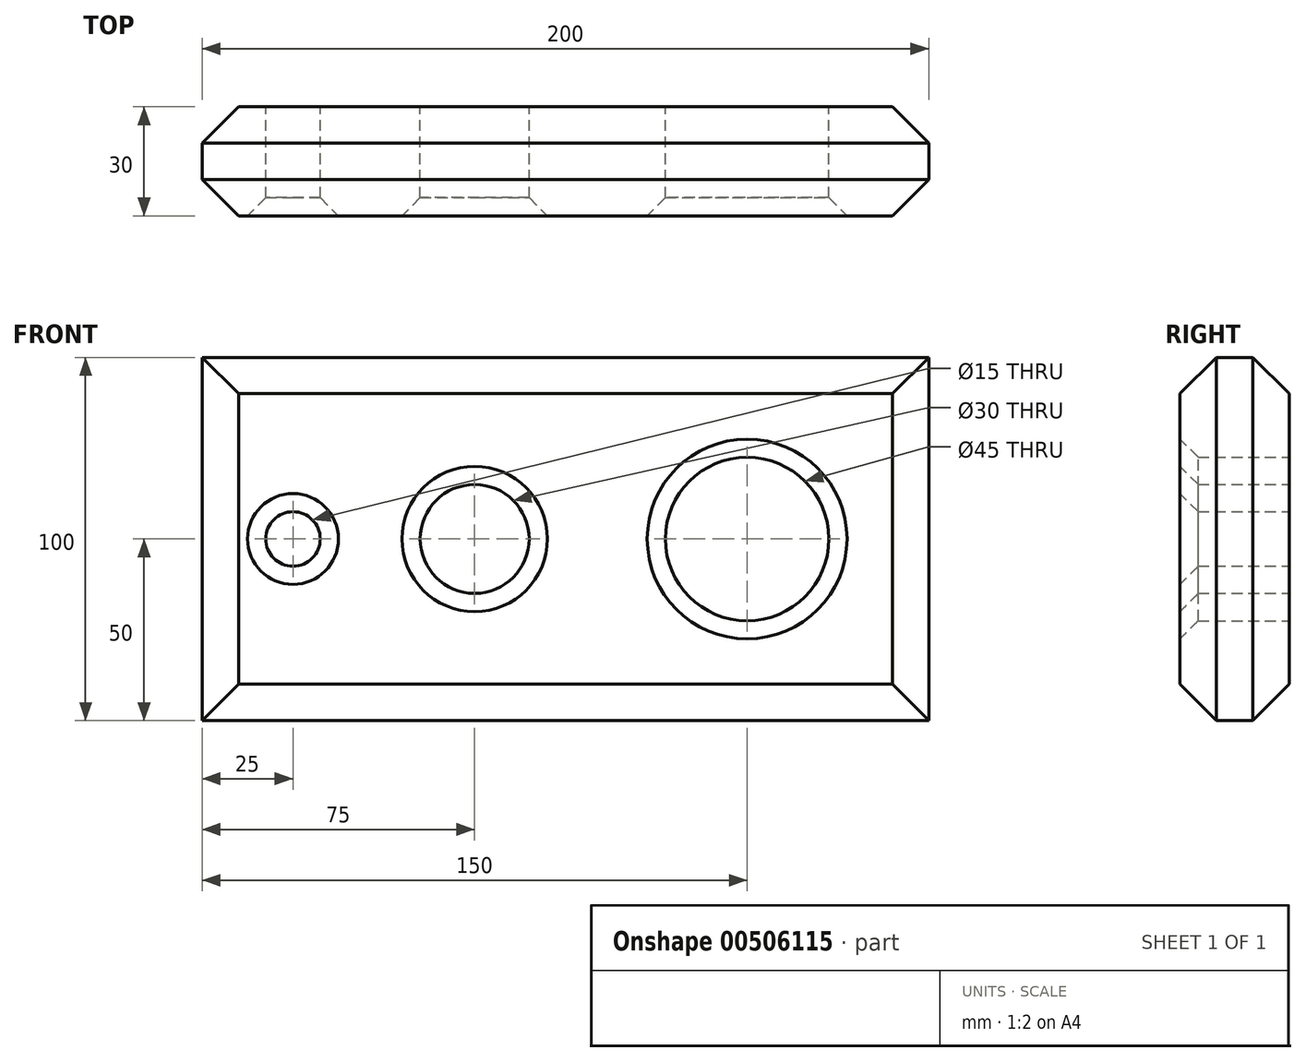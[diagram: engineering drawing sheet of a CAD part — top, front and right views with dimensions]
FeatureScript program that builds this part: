
annotation { "Feature Type Name" : "Feature", "Feature Type Description" : "" }
export const myFeature = defineFeature(function(context is Context, id is Id, definition is map)
    precondition{}
    {
        {
            var Q0;
            Q0=qCreatedBy(makeId("Front.planeOp"),FACE);
            var sketch = newSketch(context, id + "F0", { "sketchPlane" : qUnion([Q0])});
            skLineSegment(sketch, "E0.bottom", {"start": v(-100, 50) * mm, "end": v(100, 50) * mm});
            skLineSegment(sketch, "E0.top", {"start": v(-100, -50) * mm, "end": v(100, -50) * mm});
            skLineSegment(sketch, "E0.left", {"start": v(-100, 50) * mm, "end": v(-100, -50) * mm});
            skLineSegment(sketch, "E0.right", {"start": v(100, 50) * mm, "end": v(100, -50) * mm});
            skLineSegment(sketch, "E1", {"start": v(-100, 0) * mm, "end": v(-75, 0) * mm});
            skPoint(sketch, "E1.endSnap0", {"position": v(-100, 0) * mm});
            skLineSegment(sketch, "E2", {"start": v(-75, 0) * mm, "end": v(-25, 0) * mm});
            skLineSegment(sketch, "E3", {"start": v(-25, 0) * mm, "end": v(50, 0) * mm});
            skCircle(sketch, "E4", {"center": v(-75, 0) * mm, "radius": 7.5 * mm});
            skCircle(sketch, "E5", {"center": v(-25, 0) * mm, "radius": 15 * mm});
            skCircle(sketch, "E6", {"center": v(50, 0) * mm, "radius": 22.5 * mm});
            skSolve(sketch);
        }
        {
            var Q0;
            {var subQ3=sQuery(id+"F0.wireOp",EDGE,"E0.bottom");Q0=makeQuery(id+"F0.imprint","IMPRINT",FACE,{"disambiguationData":[TD([[makeQuery(id+"F0.imprint","IMPRINT",EDGE,{"derivedFrom":subQ3}),-1.0]])]});}
            extrude(context, id + "F1", {"entities" : qUnion([Q0]), "depth" : 30 * mm});
        }
        {
            var Q0;
            Q0=makeQuery(id+"F1.opExtrude","CAP_EDGE",EDGE,{"disambiguationData":[OSD([sQuery(id+"F0.wireOp",EDGE,"E0.left")])],"isStart":false});
            var Q1;
            Q1=makeQuery(id+"F1.opExtrude","CAP_EDGE",EDGE,{"disambiguationData":[OSD([sQuery(id+"F0.wireOp",EDGE,"E0.top")])],"isStart":false});
            var Q2;
            Q2=makeQuery(id+"F1.opExtrude","CAP_EDGE",EDGE,{"disambiguationData":[OSD([sQuery(id+"F0.wireOp",EDGE,"E0.right")])],"isStart":false});
            var Q3;
            Q3=makeQuery(id+"F1.opExtrude","CAP_EDGE",EDGE,{"disambiguationData":[OSD([sQuery(id+"F0.wireOp",EDGE,"E0.bottom")])],"isStart":false});
            chamfer(context, id + "F2", {"entities" : qUnion([Q0, Q1, Q2, Q3]), "width" : 10 * mm, "tangentPropagation" : true});
        }
        {
            var Q0;
            Q0=makeQuery(id+"F1.opExtrude","CAP_EDGE",EDGE,{"disambiguationData":[OSD([sQuery(id+"F0.wireOp",EDGE,"E4")])],"isStart":false});
            var Q1;
            Q1=makeQuery(id+"F1.opExtrude","CAP_EDGE",EDGE,{"disambiguationData":[OSD([sQuery(id+"F0.wireOp",EDGE,"E5")])],"isStart":false});
            var Q2;
            Q2=makeQuery(id+"F1.opExtrude","CAP_EDGE",EDGE,{"disambiguationData":[OSD([sQuery(id+"F0.wireOp",EDGE,"E6")])],"isStart":false});
            chamfer(context, id + "F3", {"entities" : qUnion([Q0, Q1, Q2]), "width" : 5 * mm, "tangentPropagation" : true});
        }
        {
            var Q0;
            Q0=makeQuery(id+"F1.opExtrude","CAP_EDGE",EDGE,{"disambiguationData":[OSD([sQuery(id+"F0.wireOp",EDGE,"E0.top")])],"isStart":true});
            var Q1;
            Q1=makeQuery(id+"F1.opExtrude","CAP_EDGE",EDGE,{"disambiguationData":[OSD([sQuery(id+"F0.wireOp",EDGE,"E0.left")])],"isStart":true});
            var Q2;
            Q2=makeQuery(id+"F1.opExtrude","CAP_EDGE",EDGE,{"disambiguationData":[OSD([sQuery(id+"F0.wireOp",EDGE,"E0.bottom")])],"isStart":true});
            var Q3;
            Q3=makeQuery(id+"F1.opExtrude","CAP_EDGE",EDGE,{"disambiguationData":[OSD([sQuery(id+"F0.wireOp",EDGE,"E0.right")])],"isStart":true});
            chamfer(context, id + "F4", {"entities" : qUnion([Q0, Q1, Q2, Q3]), "width" : 10 * mm, "tangentPropagation" : true});
        }
    });
